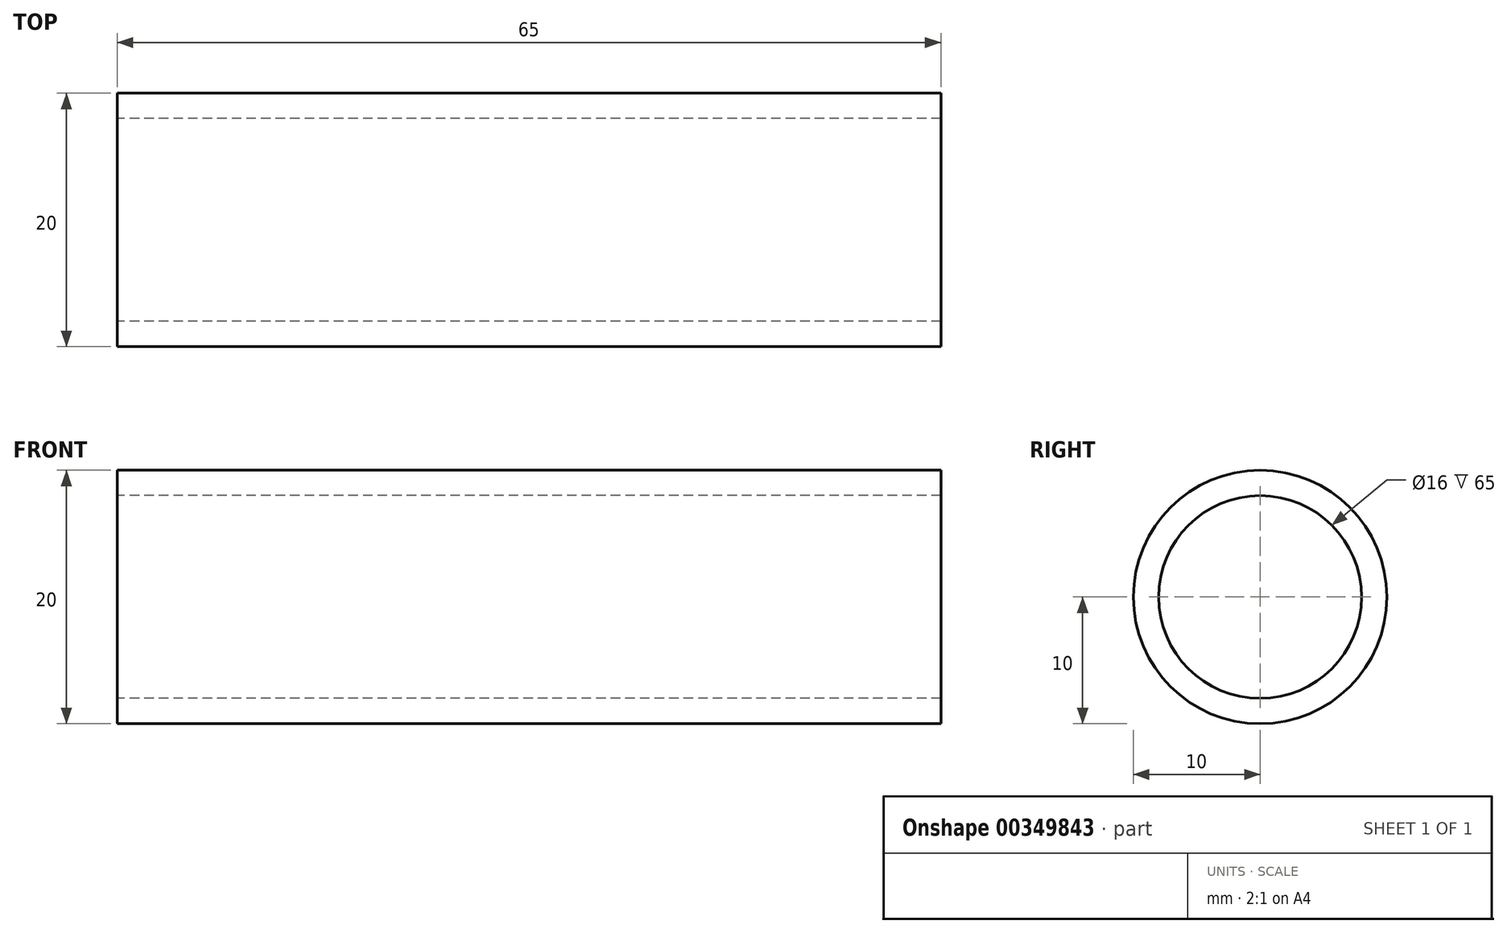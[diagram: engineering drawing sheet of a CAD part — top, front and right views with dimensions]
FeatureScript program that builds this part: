
annotation { "Feature Type Name" : "Feature", "Feature Type Description" : "" }
export const myFeature = defineFeature(function(context is Context, id is Id, definition is map)
    precondition{}
    {
        {
            var Q0;
            Q0=qCreatedBy(makeId("Right.planeOp"),FACE);
            var sketch = newSketch(context, id + "F0", { "sketchPlane" : qUnion([Q0])});
            skCircle(sketch, "E0", {"center": v(0, 0) * mm, "radius": 8 * mm});
            skCircle(sketch, "E1", {"center": v(0, 0) * mm, "radius": 10 * mm});
            skSolve(sketch);
        }
        {
            var Q0;
            Q0 = qSketchRegion(id + "F0", true);
            extrude(context, id + "F1", {"entities" : qUnion([Q0]), "depth" : 50 * mm, "hasSecondDirection" : true, "secondDirectionOppositeDirection" : true, "secondDirectionDepth" : 15 * mm});
        }
    });
